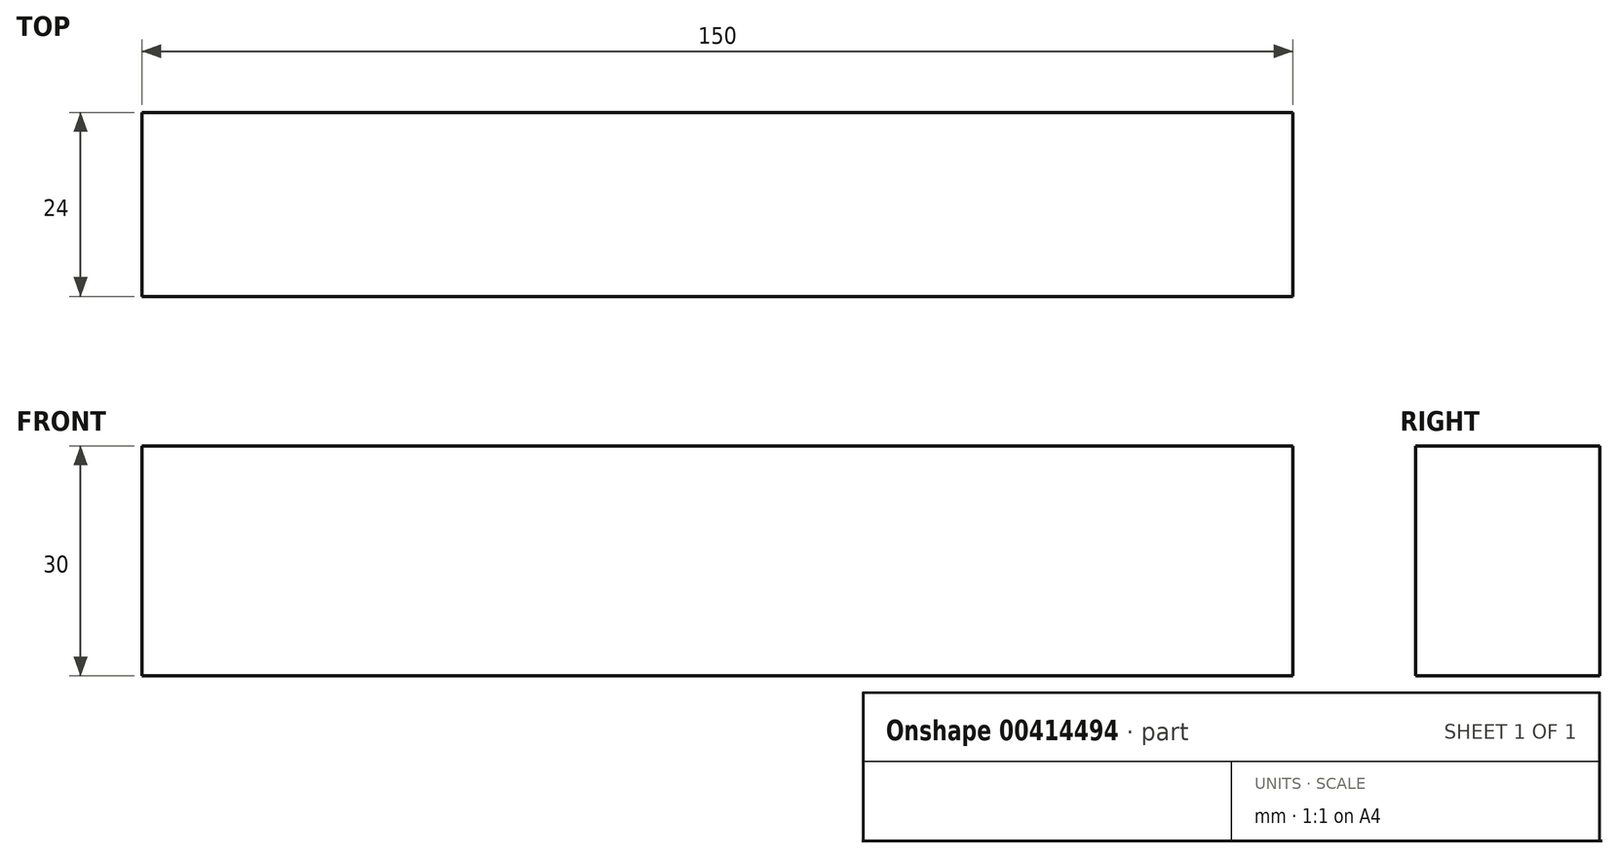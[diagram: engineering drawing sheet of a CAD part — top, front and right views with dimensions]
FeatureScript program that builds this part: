
annotation { "Feature Type Name" : "Feature", "Feature Type Description" : "" }
export const myFeature = defineFeature(function(context is Context, id is Id, definition is map)
    precondition{}
    {
        {
            var Q0;
            Q0=qCreatedBy(makeId("Top.planeOp"),FACE);
            var sketch = newSketch(context, id + "F0", { "sketchPlane" : qUnion([Q0])});
            skLineSegment(sketch, "E0.bottom", {"start": v(0, 0) * mm, "end": v(150, 0) * mm});
            skLineSegment(sketch, "E0.top", {"start": v(0, -24) * mm, "end": v(150, -24) * mm});
            skLineSegment(sketch, "E0.left", {"start": v(0, 0) * mm, "end": v(0, -24) * mm});
            skLineSegment(sketch, "E0.right", {"start": v(150, 0) * mm, "end": v(150, -24) * mm});
            skSolve(sketch);
        }
        {
            var Q0;
            Q0=makeQuery(id+"F0.imprint","IMPRINT",FACE,{"disambiguationData":[TD([[makeQuery(id+"F0.imprint","IMPRINT",EDGE,{"derivedFrom":sQuery(id+"F0.wireOp",EDGE,"E0.bottom")}),-1.0]])]});
            extrude(context, id + "F1", {"entities" : qUnion([Q0]), "depth" : 30 * mm, "offsetDistance" : 25 * mm});
        }
    });
